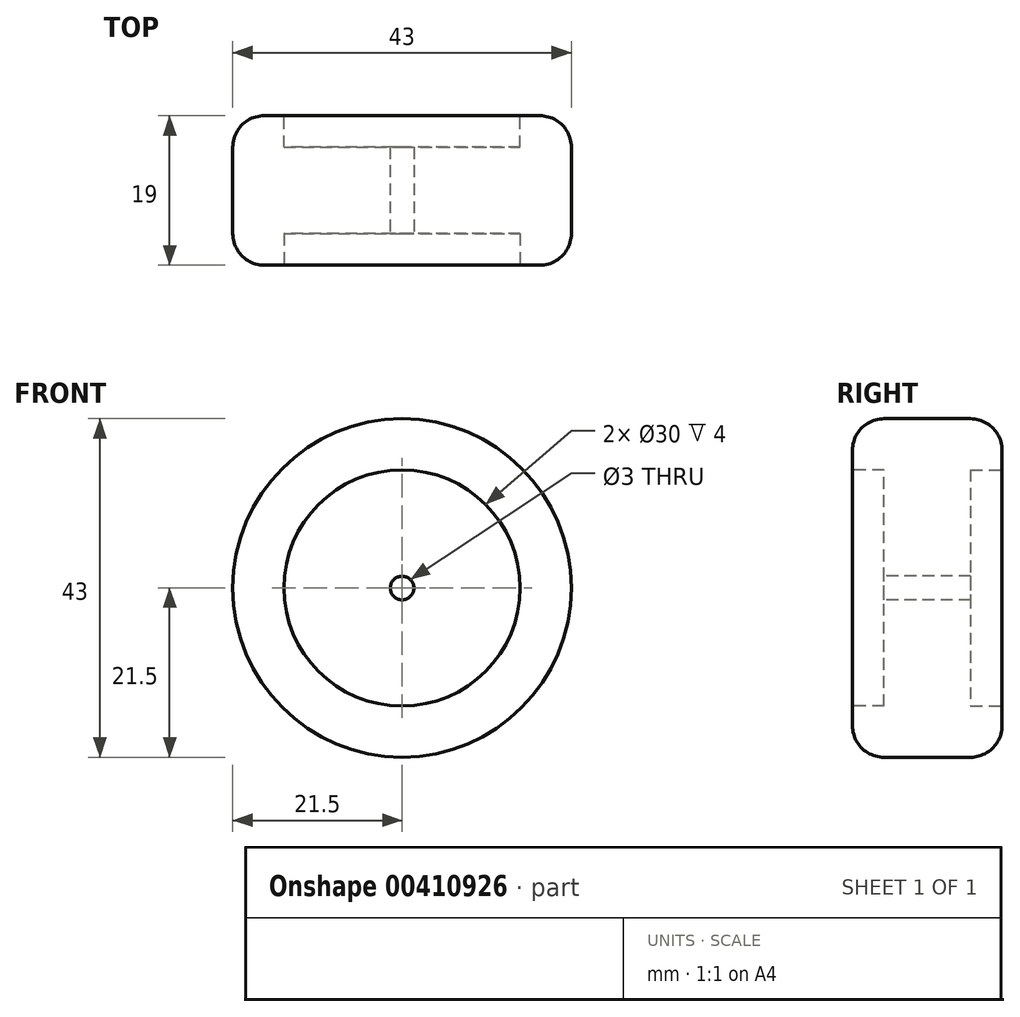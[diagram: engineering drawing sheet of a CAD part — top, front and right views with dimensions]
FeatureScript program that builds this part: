
annotation { "Feature Type Name" : "Feature", "Feature Type Description" : "" }
export const myFeature = defineFeature(function(context is Context, id is Id, definition is map)
    precondition{}
    {
        {
            var Q0;
            Q0=qCreatedBy(makeId("Front.planeOp"),FACE);
            var sketch = newSketch(context, id + "F0", { "sketchPlane" : qUnion([Q0])});
            skCircle(sketch, "E0", {"center": v(0, 0) * mm, "radius": 21.5 * mm});
            skSolve(sketch);
        }
        {
            var Q0;
            Q0 = qSketchRegion(id + "F0", true);
            extrude(context, id + "F1", {"entities" : qUnion([Q0]), "depth" : 19 * mm});
        }
        {
            var Q0;
            Q0=makeQuery(id+"F1.opExtrude","CAP_EDGE",EDGE,{"disambiguationData":[OSD([sQuery(id+"F0.wireOp",EDGE,"E0")])],"isStart":false});
            var Q1;
            Q1=makeQuery(id+"F1.opExtrude","CAP_EDGE",EDGE,{"disambiguationData":[OSD([sQuery(id+"F0.wireOp",EDGE,"E0")])],"isStart":true});
            fillet(context, id + "F2", {"entities" : qUnion([Q0, Q1]), "radius" : 4 * mm, "tangentPropagation" : true, "allowEdgeOverflow" : false});
        }
        {
            var Q0;
            Q0=makeQuery(id+"F1.opExtrude","CAP_FACE",FACE,{"disambiguationData":[OSD([sQuery(id+"F0.wireOp",EDGE,"E0")])],"isStart":false});
            var sketch = newSketch(context, id + "F3", { "sketchPlane" : qUnion([Q0])});
            skCircle(sketch, "E1", {"center": v(0, 0) * mm, "radius": 15 * mm});
            skSolve(sketch);
        }
        {
            var Q0;
            Q0 = qSketchRegion(id + "F3", true);
            extrude(context, id + "F4", {"entities" : qUnion([Q0]), "operationType" : NewBodyOperationType.REMOVE, "oppositeDirection" : true, "depth" : 4 * mm});
        }
        {
            var Q0;
            Q0=makeQuery(id+"F1.opExtrude","CAP_FACE",FACE,{"disambiguationData":[OSD([sQuery(id+"F0.wireOp",EDGE,"E0")])],"isStart":true});
            var sketch = newSketch(context, id + "F5", { "sketchPlane" : qUnion([Q0])});
            skCircle(sketch, "E2", {"center": v(0, 0) * mm, "radius": 15 * mm});
            skSolve(sketch);
        }
        {
            var Q0;
            Q0 = qSketchRegion(id + "F5", true);
            extrude(context, id + "F6", {"entities" : qUnion([Q0]), "operationType" : NewBodyOperationType.REMOVE, "oppositeDirection" : true, "depth" : 4 * mm});
        }
        {
            var Q0;
            Q0=makeQuery(id+"F4.boolean.opBoolean","COPY",FACE,{"derivedFrom":makeQuery(id+"F4.opExtrude","CAP_FACE",FACE,{"disambiguationData":[OSD([sQuery(id+"F3.wireOp",EDGE,"E1")])],"isStart":false})});
            var sketch = newSketch(context, id + "F7", { "sketchPlane" : qUnion([Q0])});
            skCircle(sketch, "E3", {"center": v(0, 0) * mm, "radius": 1.5 * mm});
            skSolve(sketch);
        }
        {
            var Q0;
            Q0 = qSketchRegion(id + "F7", true);
            extrude(context, id + "F8", {"entities" : qUnion([Q0]), "operationType" : NewBodyOperationType.REMOVE, "endBound" : BoundingType.THROUGH_ALL, "oppositeDirection" : true, "depth" : 25 * mm});
        }
    });
